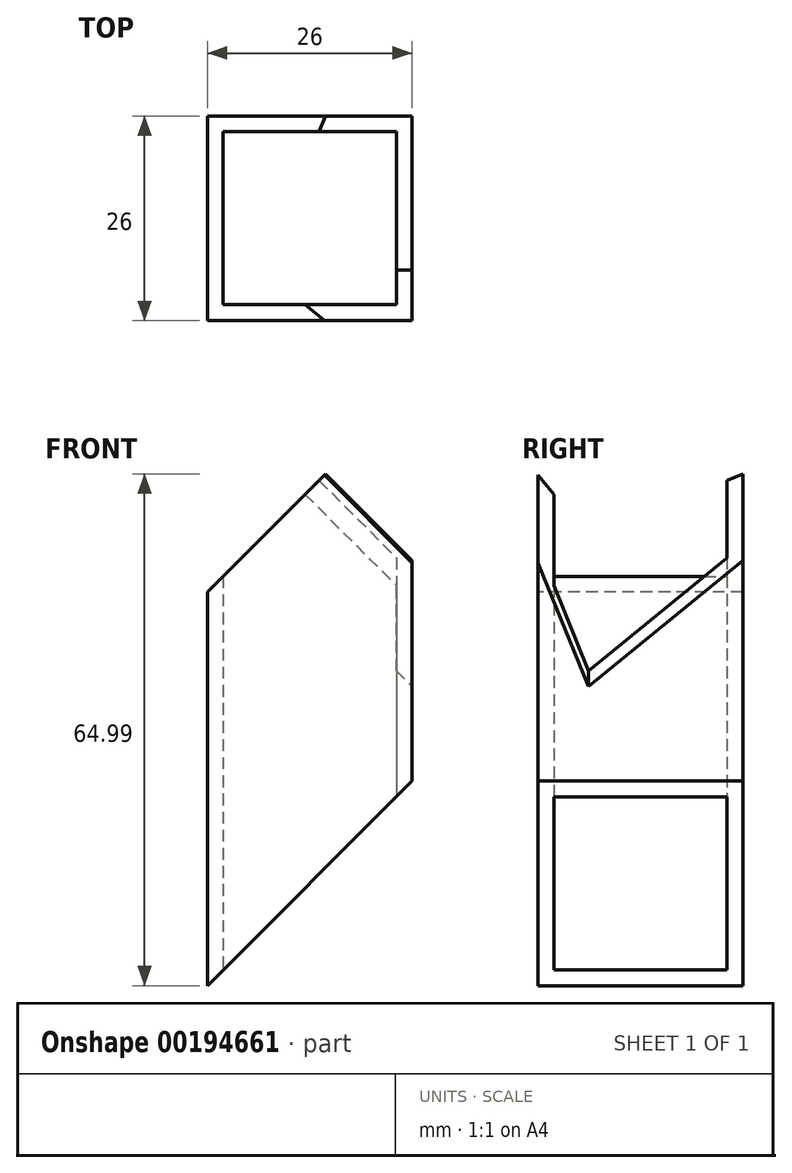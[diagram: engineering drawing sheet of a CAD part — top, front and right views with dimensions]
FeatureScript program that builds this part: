
annotation { "Feature Type Name" : "Feature", "Feature Type Description" : "" }
export const myFeature = defineFeature(function(context is Context, id is Id, definition is map)
    precondition{}
    {
        {
            var Q0;
            Q0=qCreatedBy(makeId("Top.planeOp"),FACE);
            var sketch = newSketch(context, id + "F0", { "sketchPlane" : qUnion([Q0])});
            skLineSegment(sketch, "E0.bottom", {"start": v(-13, 13) * mm, "end": v(13, 13) * mm});
            skLineSegment(sketch, "E0.top", {"start": v(-13, -13) * mm, "end": v(13, -13) * mm});
            skLineSegment(sketch, "E0.left", {"start": v(-13, 13) * mm, "end": v(-13, -13) * mm});
            skLineSegment(sketch, "E0.right", {"start": v(13, 13) * mm, "end": v(13, -13) * mm});
            skLineSegment(sketch, "E1.0", {"start": v(-11, 11) * mm, "end": v(11, 11) * mm});
            skLineSegment(sketch, "E1.1", {"start": v(-11, 11) * mm, "end": v(-11, -11) * mm});
            skLineSegment(sketch, "E1.2", {"start": v(-11, -11) * mm, "end": v(11, -11) * mm});
            skLineSegment(sketch, "E1.3", {"start": v(11, 11) * mm, "end": v(11, -11) * mm});
            skSolve(sketch);
        }
        {
            var Q0;
            Q0=makeQuery(id+"F0.imprint","IMPRINT",FACE,{"disambiguationData":[TD([[makeQuery(id+"F0.imprint","IMPRINT",EDGE,{"derivedFrom":sQuery(id+"F0.wireOp",EDGE,"E0.bottom")}),-1.0]])]});
            extrude(context, id + "F1", {"entities" : qUnion([Q0]), "depth" : 75 * mm});
        }
        {
            var Q0;
            Q0=makeQuery(id+"F1.opExtrude","SWEPT_FACE",FACE,{"disambiguationData":[OSD([sQuery(id+"F0.wireOp",EDGE,"E0.top")])]});
            var sketch = newSketch(context, id + "F2", { "sketchPlane" : qUnion([Q0])});
            skLineSegment(sketch, "E2", {"start": v(-13, 0) * mm, "end": v(13, 26) * mm});
            skLineSegment(sketch, "E3", {"start": v(13, 26) * mm, "end": v(13, 0) * mm});
            skLineSegment(sketch, "E4", {"start": v(13, 0) * mm, "end": v(-13, 0) * mm});
            skSolve(sketch);
        }
        {
            var Q0;
            Q0=makeQuery(id+"F1.opExtrude","SWEPT_FACE",FACE,{"disambiguationData":[OSD([sQuery(id+"F0.wireOp",EDGE,"E0.left")])]});
            var sketch = newSketch(context, id + "F3", { "sketchPlane" : qUnion([Q0])});
            skLineSegment(sketch, "E5", {"start": v(-13, 75) * mm, "end": v(6.5, 63.74) * mm});
            skLineSegment(sketch, "E6", {"start": v(6.5, 63.74) * mm, "end": v(13, 75) * mm});
            skLineSegment(sketch, "E7", {"start": v(13, 75) * mm, "end": v(-13, 75) * mm});
            skSolve(sketch);
        }
        {
            var Q0;
            Q0=makeQuery(id+"F1.opExtrude","SWEPT_FACE",FACE,{"disambiguationData":[OSD([sQuery(id+"F0.wireOp",EDGE,"E0.right")])]});
            var sketch = newSketch(context, id + "F4", { "sketchPlane" : qUnion([Q0])});
            skLineSegment(sketch, "E8", {"start": v(-13, 49) * mm, "end": v(13, 49) * mm, "construction": true});
            skLineSegment(sketch, "E9", {"start": v(-13, 49) * mm, "end": v(-6.5, 37.74) * mm});
            skLineSegment(sketch, "E10", {"start": v(-6.5, 37.74) * mm, "end": v(13, 49) * mm});
            skLineSegment(sketch, "E11", {"start": v(-13, 49) * mm, "end": v(13, 49) * mm});
            skLineSegment(sketch, "E12", {"start": v(-13, 37.74) * mm, "end": v(13, 37.74) * mm, "construction": true});
            skSolve(sketch);
        }
        {
            var Q0;
            Q0=makeQuery(id+"F2.imprint","IMPRINT",FACE,{"disambiguationData":[TD([[makeQuery(id+"F2.imprint","IMPRINT",EDGE,{"derivedFrom":sQuery(id+"F2.wireOp",EDGE,"E2")}),-1.0]])]});
            extrude(context, id + "F5", {"entities" : qUnion([Q0]), "operationType" : NewBodyOperationType.REMOVE, "endBound" : BoundingType.THROUGH_ALL, "oppositeDirection" : true, "depth" : 25.4 * mm});
        }
        {
            var Q0;
            Q0=makeQuery(id+"F1.opExtrude","SWEPT_FACE",FACE,{"disambiguationData":[OSD([sQuery(id+"F0.wireOp",EDGE,"E0.top")])]});
            var sketch = newSketch(context, id + "F6", { "sketchPlane" : qUnion([Q0])});
            skPoint(sketch, "E13", {"position": v(13, 38) * mm});
            skLineSegment(sketch, "E14", {"start": v(13, 38) * mm, "end": v(-13, 12) * mm});
            skSolve(sketch);
        }
        {
            var Q0;
            Q0=sQuery(id+"F6.wireOp",EDGE,"E14");
            var Q1;
            Q1=sQuery(id+"F4.wireOp",EDGE,"E12");
            cPlane(context, id + "F7", {"entities" : qUnion([Q0, Q1]), "cplaneType" : CPlaneType.LINE_ANGLE, "offset" : 25.4 * mm, "angle" : 0 * degree, "width" : 152.4 * mm, "height" : 152.4 * mm});
        }
        {
            var Q0;
            Q0=qCreatedBy(id+"F7.planeOp",FACE);
            var sketch = newSketch(context, id + "F8", { "sketchPlane" : qUnion([Q0])});
            skLineSegment(sketch, "E15", {"start": v(-6.58, 36.06) * mm, "end": v(-13, 47.18) * mm});
            skLineSegment(sketch, "E16", {"start": v(13, 47.37) * mm, "end": v(-6.58, 36.06) * mm});
            skLineSegment(sketch, "E17", {"start": v(-13, 47.18) * mm, "end": v(-13, 69.7) * mm});
            skLineSegment(sketch, "E18", {"start": v(13, 47.37) * mm, "end": v(13, 69.7) * mm});
            skLineSegment(sketch, "E19", {"start": v(-13, 69.7) * mm, "end": v(13, 69.7) * mm});
            skSolve(sketch);
        }
        {
            var Q0;
            Q0=makeQuery(id+"F8.imprint","IMPRINT",FACE,{"disambiguationData":[TD([[makeQuery(id+"F8.imprint","IMPRINT",EDGE,{"derivedFrom":sQuery(id+"F8.wireOp",EDGE,"E15")}),-1.0]])]});
            extrude(context, id + "F9", {"entities" : qUnion([Q0]), "operationType" : NewBodyOperationType.REMOVE, "endBound" : BoundingType.THROUGH_ALL, "oppositeDirection" : true, "depth" : 25.4 * mm});
        }
        {
            var Q0;
            {var subQ0=sQuery(id+"F6.wireOp",EDGE,"E14");Q0=makeQuery(id+"F6.imprint","IMPRINT",FACE,{"disambiguationData":[TD([[makeQuery(id+"F6.imprint","IMPRINT",EDGE,{"derivedFrom":subQ0}),-1.0]])]});}
            var sketch = newSketch(context, id + "F10", { "sketchPlane" : qUnion([Q0])});
            skLineSegment(sketch, "E20", {"start": v(-13, 50) * mm, "end": v(-13, 87.2) * mm});
            skLineSegment(sketch, "E21", {"start": v(-13, 50) * mm, "end": v(20.82, 83.82) * mm});
            skLineSegment(sketch, "E22", {"start": v(20.82, 83.82) * mm, "end": v(20.82, 87.2) * mm});
            skLineSegment(sketch, "E23", {"start": v(-13, 87.2) * mm, "end": v(20.82, 87.2) * mm});
            skSolve(sketch);
        }
        {
            var Q0;
            Q0 = qSketchRegion(id + "F10", true);
            extrude(context, id + "F11", {"entities" : qUnion([Q0]), "operationType" : NewBodyOperationType.REMOVE, "endBound" : BoundingType.THROUGH_ALL, "oppositeDirection" : true, "depth" : 25.4 * mm});
        }
    });
